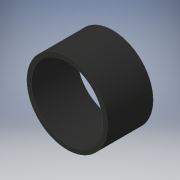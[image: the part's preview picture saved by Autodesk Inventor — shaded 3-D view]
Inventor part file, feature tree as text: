
AUTODESK INVENTOR PART (.ipt)
format: ipt  version: 2018 (Build 220112000, 112)  size: 126,464 bytes
history: native  units: in
note: dims shown in document units (in); Inventor stores cm internally (conversion verified against a paired STEP export)
features: extrude x1, sketch x1
ambient origin geometry x8: Origin, YZ Plane, XZ Plane, XY Plane, X Axis, Y Axis, Z Axis, Center Point
bodies: Solid1 (feature_tree)
feature tree (2):
  extrude  "Extrusion1"  Depth=2.55in TaperAngle=0.0deg
  sketch  "Sketch1"  dims[d1=0.25in d2=2.55in d3=0.0in d4=4.0in]
